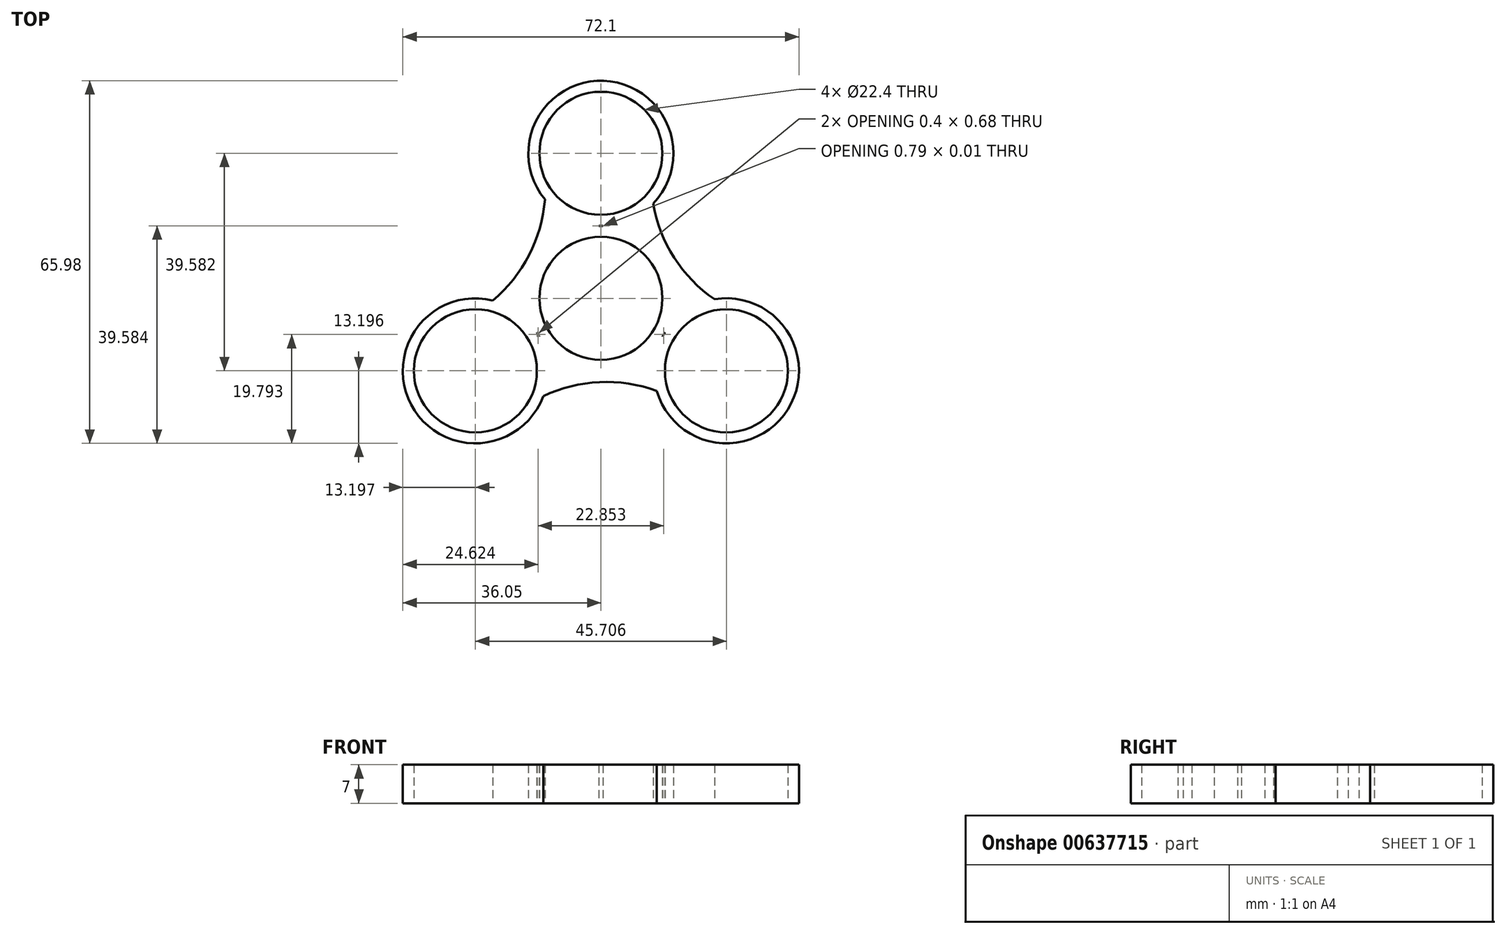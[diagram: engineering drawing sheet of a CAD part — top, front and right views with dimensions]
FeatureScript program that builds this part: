
annotation { "Feature Type Name" : "Feature", "Feature Type Description" : "" }
export const myFeature = defineFeature(function(context is Context, id is Id, definition is map)
    precondition{}
    {
        {
            var Q0;
            Q0=qCreatedBy(makeId("Top.planeOp"),FACE);
            var sketch = newSketch(context, id + "F0", { "sketchPlane" : qUnion([Q0])});
            skCircle(sketch, "E0", {"center": v(0, 0) * mm, "radius": 11.2 * mm});
            skArc(sketch, "E1", {"start": v(-11.62, -6.25) * mm, "mid": v(-11.43, -6.6) * mm, "end": v(-11.23, -6.94) * mm});
            skCircle(sketch, "E2", {"center": v(0, 26.39) * mm, "radius": 11.2 * mm});
            skArc(sketch, "E3", {"start": v(9.5, 17.22) * mm, "mid": v(0.51, 39.58) * mm, "end": v(-10.18, 17.99) * mm});
            skCircle(sketch, "E4.1.0", {"center": v(-22.85, -13.2) * mm, "radius": 11.2 * mm});
            skArc(sketch, "E4.1.1", {"start": v(-19.67, -0.38) * mm, "mid": v(-34.53, -19.35) * mm, "end": v(-10.49, -17.81) * mm});
            skCircle(sketch, "E4.2.0", {"center": v(22.85, -13.2) * mm, "radius": 11.2 * mm});
            skArc(sketch, "E4.2.1", {"start": v(11.62, -6.25) * mm, "mid": v(11.42, -6.6) * mm, "end": v(11.23, -6.94) * mm});
            skArc(sketch, "E5", {"start": v(-19.67, -0.38) * mm, "mid": v(-13.09, 7.85) * mm, "end": v(-10.18, 17.99) * mm});
            skArc(sketch, "E6.1.0", {"start": v(10.17, -16.84) * mm, "mid": v(-0.26, -15.26) * mm, "end": v(-10.49, -17.81) * mm});
            skArc(sketch, "E6.2.0", {"start": v(9.5, 17.22) * mm, "mid": v(13.34, 7.4) * mm, "end": v(20.67, -0.18) * mm});
            skArc(sketch, "E7.trimOffspring", {"start": v(0.4, 13.2) * mm, "mid": v(0, 13.2) * mm, "end": v(-0.4, 13.2) * mm});
            skArc(sketch, "E8.trimOffspring", {"start": v(11.23, -6.94) * mm, "mid": v(11.43, -6.6) * mm, "end": v(11.62, -6.25) * mm});
            skArc(sketch, "E9.trimOffspring", {"start": v(-0.4, 13.2) * mm, "mid": v(0, 13.19) * mm, "end": v(0.4, 13.2) * mm});
            skArc(sketch, "E10.trimOffspring", {"start": v(-11.23, -6.94) * mm, "mid": v(-11.42, -6.6) * mm, "end": v(-11.62, -6.25) * mm});
            skArc(sketch, "E11.trimOffspring", {"start": v(10.17, -16.84) * mm, "mid": v(34.02, -20.23) * mm, "end": v(20.67, -0.18) * mm});
            skSolve(sketch);
        }
        {
            var Q0;
            Q0=qCreatedBy(makeId("Top.planeOp"),FACE);
            var sketch = newSketch(context, id + "F1", { "sketchPlane" : qUnion([Q0])});
            skSolve(sketch);
        }
        {
            var Q0;
            Q0 = qSketchRegion(id + "F1", true);
            var Q1;
            Q1=makeQuery(id+"F0.imprint","IMPRINT",FACE,{"disambiguationData":[TD([[makeQuery(id+"F0.imprint","IMPRINT",EDGE,{"derivedFrom":sQuery(id+"F0.wireOp",EDGE,"E0")}),-1.0]])]});
            extrude(context, id + "F2", {"entities" : qUnion([Q0, Q1]), "depth" : 7 * mm, "offsetDistance" : 25 * mm});
        }
    });
